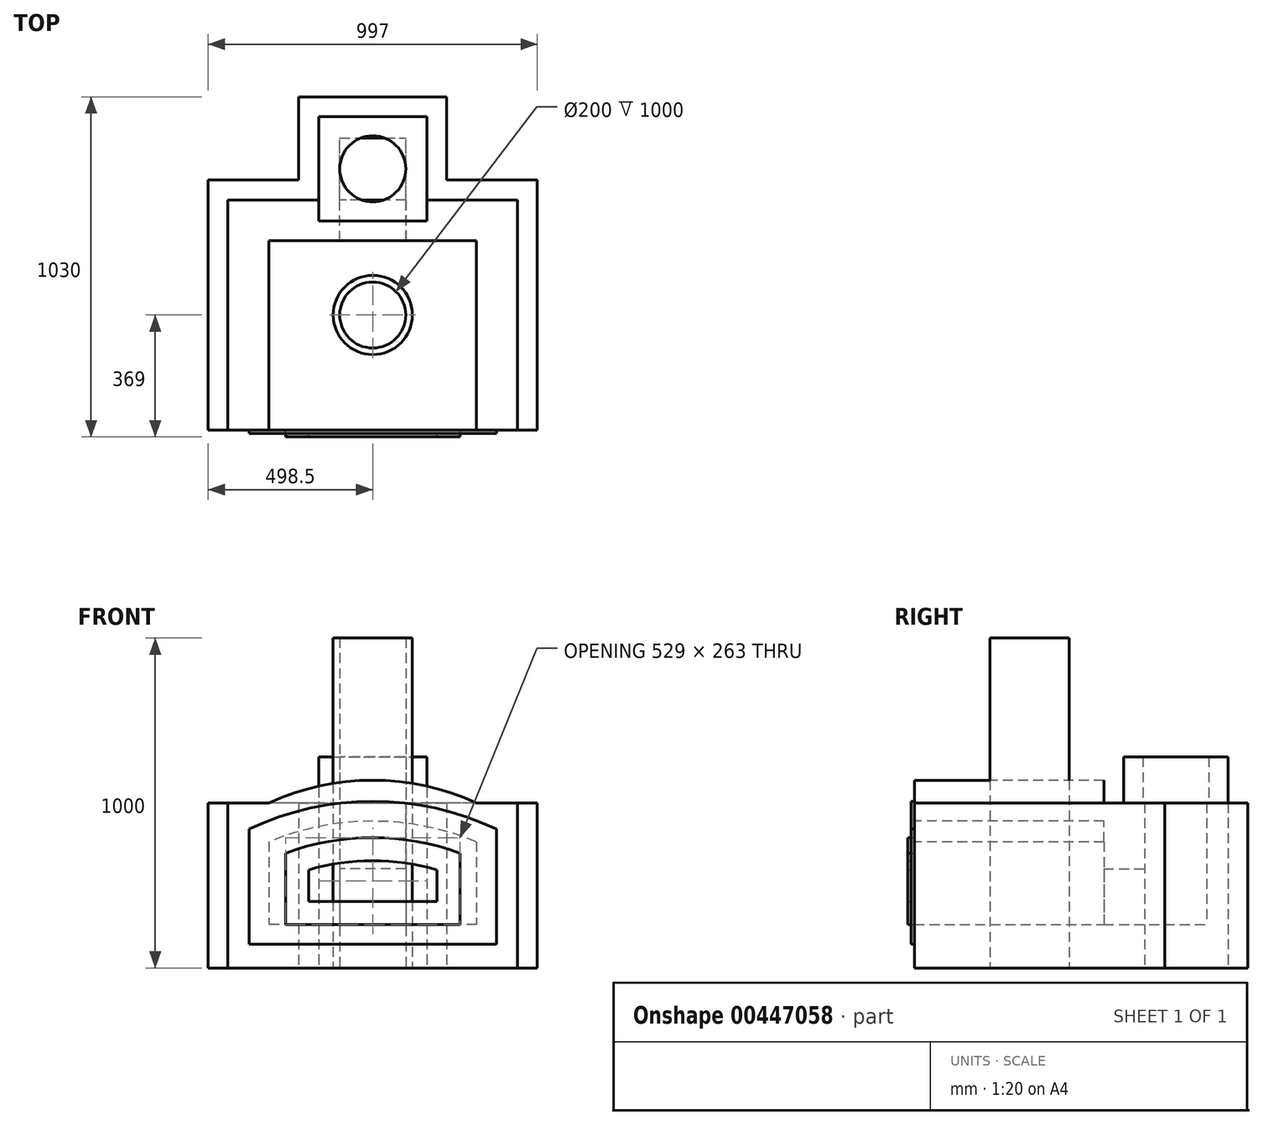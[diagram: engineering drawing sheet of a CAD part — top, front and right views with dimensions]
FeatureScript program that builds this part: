
annotation { "Feature Type Name" : "Feature", "Feature Type Description" : "" }
export const myFeature = defineFeature(function(context is Context, id is Id, definition is map)
    precondition{}
    {
        {
            var Q0;
            Q0=qCreatedBy(makeId("Top.planeOp"),FACE);
            var sketch = newSketch(context, id + "F0", { "sketchPlane" : qUnion([Q0])});
            skLineSegment(sketch, "E0.bottom", {"start": v(438.5, -349) * mm, "end": v(-438.5, -349) * mm});
            skLineSegment(sketch, "E0.top", {"start": v(438.5, 349) * mm, "end": v(164, 349) * mm});
            skLineSegment(sketch, "E0.left", {"start": v(438.5, -349) * mm, "end": v(438.5, 349) * mm});
            skLineSegment(sketch, "E0.right", {"start": v(-438.5, -349) * mm, "end": v(-438.5, 349) * mm});
            skPoint(sketch, "E0.middle", {"position": v(0, 0) * mm});
            skLineSegment(sketch, "E1.top", {"start": v(-164, 601) * mm, "end": v(164, 601) * mm});
            skLineSegment(sketch, "E1.left", {"start": v(-164, 349) * mm, "end": v(-164, 601) * mm});
            skLineSegment(sketch, "E1.right", {"start": v(164, 349) * mm, "end": v(164, 601) * mm});
            skLineSegment(sketch, "E2.trimOffspring", {"start": v(-164, 349) * mm, "end": v(-438.5, 349) * mm});
            skSolve(sketch);
        }
        {
            var Q0;
            Q0=makeQuery(id+"F0.imprint","IMPRINT",FACE,{"disambiguationData":[TD([[makeQuery(id+"F0.imprint","IMPRINT",EDGE,{"derivedFrom":sQuery(id+"F0.wireOp",EDGE,"E0.bottom")}),-1.0]])]});
            extrude(context, id + "F1", {"entities" : qUnion([Q0]), "depth" : (64 + 64 + 4) * mm});
        }
        {
            var Q0;
            Q0=makeQuery(id+"F1.opExtrude","CAP_FACE",FACE,{"disambiguationData":[OSD([sQuery(id+"F0.wireOp",EDGE,"E0.bottom"),sQuery(id+"F0.wireOp",EDGE,"E0.top"),sQuery(id+"F0.wireOp",EDGE,"E0.left"),sQuery(id+"F0.wireOp",EDGE,"E0.right"),sQuery(id+"F0.wireOp",EDGE,"E1.top"),sQuery(id+"F0.wireOp",EDGE,"E1.left"),sQuery(id+"F0.wireOp",EDGE,"E1.right"),sQuery(id+"F0.wireOp",EDGE,"E2.trimOffspring")])],"isStart":false});
            var sketch = newSketch(context, id + "F2", { "sketchPlane" : qUnion([Q0])});
            skLineSegment(sketch, "E3.0", {"start": v(314.5, -474) * mm, "end": v(314.5, 225) * mm});
            skLineSegment(sketch, "E3.1", {"start": v(314.5, 225) * mm, "end": v(100, 225) * mm});
            skLineSegment(sketch, "E3.2", {"start": v(100, 225) * mm, "end": v(100, 537) * mm});
            skLineSegment(sketch, "E3.3", {"start": v(-314.5, -474) * mm, "end": v(-314.5, 225) * mm});
            skLineSegment(sketch, "E3.4", {"start": v(-100, 225) * mm, "end": v(-314.5, 225) * mm});
            skLineSegment(sketch, "E3.5", {"start": v(-100, 225) * mm, "end": v(-100, 537) * mm});
            skLineSegment(sketch, "E3.6", {"start": v(-100, 537) * mm, "end": v(100, 537) * mm});
            skSolve(sketch);
        }
        {
            var Q0;
            {var subQ2=sQuery(id+"F2.wireOp",EDGE,"E3.0");Q0=makeQuery(id+"F2.imprint","IMPRINT",FACE,{"disambiguationData":[TD([[makeQuery(id+"F2.imprint","IMPRINT",EDGE,{"derivedFrom":subQ2}),-1.0]])]});}
            extrude(context, id + "F3", {"entities" : qUnion([Q0]), "operationType" : NewBodyOperationType.ADD, "depth" : (500 - 64 - 64 - 4) * mm});
        }
        {
            var Q0;
            {var subQ0=sQuery(id+"F0.wireOp",EDGE,"E0.bottom");var subQ1=makeQuery(id+"F1.opExtrude","CAP_EDGE",EDGE,{"disambiguationData":[OSD([subQ0])],"isStart":false});Q0=makeQuery(id+"F3.boolean.opBoolean","MERGE",FACE,{"derivedFrom":[makeQuery(id+"F1.opExtrude","SWEPT_FACE",FACE,{"disambiguationData":[OSD([subQ0])]}),makeQuery(id+"F3.opExtrude","SWEPT_FACE",FACE,{"disambiguationData":[OSD([subQ0]),TDD([makeQuery(id+"F2.imprint","IMPRINT",EDGE,{"disambiguationData":[TD([[makeQuery(id+"F2.imprint","INTERSECT",VERTEX,{"derivedFrom":[subQ1,makeQuery(id+"F1.opExtrude","CAP_EDGE",EDGE,{"disambiguationData":[OSD([sQuery(id+"F0.wireOp",EDGE,"E0.left")])],"isStart":false})]}),-1.0]])],"derivedFrom":subQ1})])]}),makeQuery(id+"F3.opExtrude","SWEPT_FACE",FACE,{"disambiguationData":[OSD([subQ0]),TDD([makeQuery(id+"F2.imprint","IMPRINT",EDGE,{"disambiguationData":[TD([[makeQuery(id+"F2.imprint","INTERSECT",VERTEX,{"derivedFrom":[subQ1,makeQuery(id+"F1.opExtrude","CAP_EDGE",EDGE,{"disambiguationData":[OSD([sQuery(id+"F0.wireOp",EDGE,"E0.right")])],"isStart":false})]}),1.0]])],"derivedFrom":subQ1})])]})]});}
            var sketch = newSketch(context, id + "F4", { "sketchPlane" : qUnion([Q0])});
            skLineSegment(sketch, "E4", {"start": v(-314.5, 382) * mm, "end": v(314.5, 382) * mm, "construction": true});
            skLineSegment(sketch, "E5", {"start": v(0, 382) * mm, "end": v(0, 445) * mm, "construction": true});
            skArc(sketch, "E6", {"start": v(314.5, 382) * mm, "mid": v(0, 445) * mm, "end": v(-314.5, 382) * mm});
            skLineSegment(sketch, "E7", {"start": v(0, 569) * mm, "end": v(0, 500) * mm, "construction": true});
            skPoint(sketch, "E7.startSnap0", {"position": v(0, 132) * mm});
            skArc(sketch, "E8", {"start": v(314.5, 500) * mm, "mid": v(0, 569) * mm, "end": v(-314.5, 500) * mm});
            skLineSegment(sketch, "E9", {"start": v(-314.5, 500) * mm, "end": v(-314.5, 382) * mm});
            skLineSegment(sketch, "E10", {"start": v(314.5, 500) * mm, "end": v(314.5, 382) * mm});
            skSolve(sketch);
        }
        {
            var Q0;
            Q0=makeQuery(id+"F4.imprint","IMPRINT",FACE,{"disambiguationData":[TD([[makeQuery(id+"F4.imprint","IMPRINT",EDGE,{"derivedFrom":sQuery(id+"F4.wireOp",EDGE,"E6")}),-1.0]])]});
            var Q1;
            Q1=makeQuery(id+"F3.opExtrude","SWEPT_FACE",FACE,{"disambiguationData":[OSD([sQuery(id+"F2.wireOp",EDGE,"E3.4")])]});
            extrude(context, id + "F5", {"entities" : qUnion([Q0]), "operationType" : NewBodyOperationType.ADD, "endBound" : BoundingType.UP_TO_SURFACE, "oppositeDirection" : true, "endBoundEntityFace" : qUnion([Q1]), "depth" : 25 * mm});
        }
        {
            var Q0;
            Q0=makeQuery(id+"F3.opExtrude","SWEPT_FACE",FACE,{"disambiguationData":[OSD([sQuery(id+"F2.wireOp",EDGE,"E3.5")])]});
            var sketch = newSketch(context, id + "F6", { "sketchPlane" : qUnion([Q0])});
            skLineSegment(sketch, "E11.bottom", {"start": v(225, 500) * mm, "end": v(349, 500) * mm});
            skLineSegment(sketch, "E11.top", {"start": v(225, 300) * mm, "end": v(349, 300) * mm});
            skLineSegment(sketch, "E11.left", {"start": v(225, 500) * mm, "end": v(225, 300) * mm});
            skLineSegment(sketch, "E11.right", {"start": v(349, 500) * mm, "end": v(349, 300) * mm});
            skSolve(sketch);
        }
        {
            var Q0;
            {var subQ5=sQuery(id+"F6.wireOp",EDGE,"E11.bottom");Q0=makeQuery(id+"F6.imprint","IMPRINT",FACE,{"disambiguationData":[TD([[makeQuery(id+"F6.imprint","IMPRINT",EDGE,{"derivedFrom":subQ5}),-1.0]])]});}
            var Q1;
            Q1=makeQuery(id+"F3.opExtrude","SWEPT_FACE",FACE,{"disambiguationData":[OSD([sQuery(id+"F2.wireOp",EDGE,"E3.2")])]});
            extrude(context, id + "F7", {"entities" : qUnion([Q0]), "operationType" : NewBodyOperationType.ADD, "endBound" : BoundingType.UP_TO_SURFACE, "endBoundEntityFace" : qUnion([Q1]), "depth" : 25 * mm});
        }
        {
            var Q0;
            Q0=makeQuery(id+"F7.boolean.opBoolean","MERGE",FACE,{"derivedFrom":[makeQuery(id+"F3.opExtrude","CAP_FACE",FACE,{"disambiguationData":[OSD([sQuery(id+"F0.wireOp",EDGE,"E0.bottom"),sQuery(id+"F0.wireOp",EDGE,"E0.top"),sQuery(id+"F0.wireOp",EDGE,"E0.left"),sQuery(id+"F0.wireOp",EDGE,"E0.right"),sQuery(id+"F0.wireOp",EDGE,"E1.top"),sQuery(id+"F0.wireOp",EDGE,"E1.left"),sQuery(id+"F0.wireOp",EDGE,"E1.right"),sQuery(id+"F0.wireOp",EDGE,"E2.trimOffspring"),sQuery(id+"F2.wireOp",EDGE,"E3.0"),sQuery(id+"F2.wireOp",EDGE,"E3.1"),sQuery(id+"F2.wireOp",EDGE,"E3.2"),sQuery(id+"F2.wireOp",EDGE,"E3.3"),sQuery(id+"F2.wireOp",EDGE,"E3.4"),sQuery(id+"F2.wireOp",EDGE,"E3.5"),sQuery(id+"F2.wireOp",EDGE,"E3.6")])],"isStart":false}),makeQuery(id+"F7.opExtrude","SWEPT_FACE",FACE,{"disambiguationData":[OSD([sQuery(id+"F6.wireOp",EDGE,"E11.bottom")])]})]});
            var sketch = newSketch(context, id + "F8", { "sketchPlane" : qUnion([Q0])});
            skLineSegment(sketch, "E12.bottom", {"start": v(-164, 601) * mm, "end": v(164, 601) * mm});
            skLineSegment(sketch, "E12.top", {"start": v(-164, 285) * mm, "end": v(164, 285) * mm});
            skLineSegment(sketch, "E12.left", {"start": v(-164, 601) * mm, "end": v(-164, 285) * mm});
            skLineSegment(sketch, "E12.right", {"start": v(164, 601) * mm, "end": v(164, 285) * mm});
            skCircle(sketch, "E13", {"center": v(0, 443) * mm, "radius": 100 * mm});
            skPoint(sketch, "E13.centerSnap0", {"position": v(100, 443) * mm});
            skPoint(sketch, "E13.centerSnap1", {"position": v(0, 349) * mm});
            skSolve(sketch);
        }
        {
            var Q0;
            {var subQ0=sQuery(id+"F8.wireOp",EDGE,"E13");var subQ1=makeQuery(id+"F3.opExtrude","CAP_EDGE",EDGE,{"disambiguationData":[OSD([sQuery(id+"F2.wireOp",EDGE,"E3.6")])],"isStart":false});var subQ2=makeQuery(id+"F8.imprint","INTERSECT",VERTEX,{"disambiguationData":[OD(1.0)],"derivedFrom":[subQ1,subQ0]});Q0=makeQuery(id+"F8.imprint","IMPRINT",FACE,{"disambiguationData":[TD([[makeQuery(id+"F8.imprint","IMPRINT",EDGE,{"disambiguationData":[TD([[subQ2,-1.0]])],"derivedFrom":subQ0}),-1.0]])]});}
            var Q1;
            {var subQ18=sQuery(id+"F8.wireOp",EDGE,"E12.bottom");Q1=makeQuery(id+"F8.imprint","IMPRINT",FACE,{"disambiguationData":[TD([[makeQuery(id+"F8.imprint","IMPRINT",EDGE,{"derivedFrom":subQ18}),-1.0]])]});}
            var Q2;
            {var subQ0=sQuery(id+"F8.wireOp",EDGE,"E13");var subQ1=makeQuery(id+"F3.opExtrude","CAP_EDGE",EDGE,{"disambiguationData":[OSD([sQuery(id+"F2.wireOp",EDGE,"E3.2")])],"isStart":false});var subQ2=makeQuery(id+"F8.imprint","INTERSECT",VERTEX,{"derivedFrom":[subQ1,subQ0]});Q2=makeQuery(id+"F8.imprint","IMPRINT",FACE,{"disambiguationData":[TD([[makeQuery(id+"F8.imprint","IMPRINT",EDGE,{"disambiguationData":[TD([[subQ2,1.0]])],"derivedFrom":subQ0}),-1.0]])]});}
            var Q3;
            {var subQ0=sQuery(id+"F8.wireOp",EDGE,"E13");var subQ1=makeQuery(id+"F3.opExtrude","CAP_EDGE",EDGE,{"disambiguationData":[OSD([sQuery(id+"F2.wireOp",EDGE,"E3.6")])],"isStart":false});var subQ2=makeQuery(id+"F8.imprint","INTERSECT",VERTEX,{"disambiguationData":[OD(0.0)],"derivedFrom":[subQ1,subQ0]});Q3=makeQuery(id+"F8.imprint","IMPRINT",FACE,{"disambiguationData":[TD([[makeQuery(id+"F8.imprint","IMPRINT",EDGE,{"disambiguationData":[TD([[subQ2,1.0]])],"derivedFrom":subQ0}),-1.0]])]});}
            var Q4;
            {var subQ0=sQuery(id+"F8.wireOp",EDGE,"E13");var subQ1=sQuery(id+"F2.wireOp",EDGE,"E3.5");var subQ2=makeQuery(id+"F3.opExtrude","CAP_EDGE",EDGE,{"disambiguationData":[OSD([subQ1])],"isStart":false});var subQ3=makeQuery(id+"F8.imprint","INTERSECT",VERTEX,{"derivedFrom":[subQ2,subQ0]});Q4=makeQuery(id+"F8.imprint","IMPRINT",FACE,{"disambiguationData":[TD([[makeQuery(id+"F8.imprint","IMPRINT",EDGE,{"disambiguationData":[TD([[subQ3,-1.0]])],"derivedFrom":subQ0}),-1.0]])]});}
            extrude(context, id + "F9", {"entities" : qUnion([Q0, Q1, Q2, Q3, Q4]), "operationType" : NewBodyOperationType.ADD, "depth" : (89 + 50) * mm});
        }
        {
            var Q0;
            Q0=qCreatedBy(makeId("Top.planeOp"),FACE);
            var sketch = newSketch(context, id + "F10", { "sketchPlane" : qUnion([Q0])});
            skCircle(sketch, "E14", {"center": v(0, 0) * mm, "radius": 120 * mm});
            skCircle(sketch, "E15", {"center": v(0, 0) * mm, "radius": 100 * mm});
            skSolve(sketch);
        }
        {
            var Q0;
            Q0=makeQuery(id+"F10.imprint","IMPRINT",FACE,{"disambiguationData":[TD([[makeQuery(id+"F10.imprint","IMPRINT",EDGE,{"derivedFrom":sQuery(id+"F10.wireOp",EDGE,"E14")}),1.0]])]});
            extrude(context, id + "F11", {"entities" : qUnion([Q0]), "depth" : 1000 * mm});
        }
        {
            var Q0;
            Q0=makeQuery(id+"F1.opExtrude","CAP_FACE",FACE,{"disambiguationData":[OSD([sQuery(id+"F0.wireOp",EDGE,"E0.bottom"),sQuery(id+"F0.wireOp",EDGE,"E0.top"),sQuery(id+"F0.wireOp",EDGE,"E0.left"),sQuery(id+"F0.wireOp",EDGE,"E0.right"),sQuery(id+"F0.wireOp",EDGE,"E1.top"),sQuery(id+"F0.wireOp",EDGE,"E1.left"),sQuery(id+"F0.wireOp",EDGE,"E1.right"),sQuery(id+"F0.wireOp",EDGE,"E2.trimOffspring")])],"isStart":true});
            var sketch = newSketch(context, id + "F12", { "sketchPlane" : qUnion([Q0])});
            skLineSegment(sketch, "E16.0", {"start": v(498.5, 349) * mm, "end": v(498.5, -409) * mm});
            skLineSegment(sketch, "E16.1", {"start": v(498.5, -409) * mm, "end": v(224, -409) * mm});
            skLineSegment(sketch, "E16.2", {"start": v(224, -409) * mm, "end": v(224, -661) * mm});
            skLineSegment(sketch, "E16.3", {"start": v(-498.5, 349) * mm, "end": v(-498.5, -409) * mm});
            skLineSegment(sketch, "E16.4", {"start": v(-224, -409) * mm, "end": v(-498.5, -409) * mm});
            skLineSegment(sketch, "E16.5", {"start": v(-224, -409) * mm, "end": v(-224, -661) * mm});
            skLineSegment(sketch, "E16.6", {"start": v(-224, -661) * mm, "end": v(224, -661) * mm});
            skLineSegment(sketch, "E17", {"start": v(-438.5, 349) * mm, "end": v(-498.5, 349) * mm});
            skLineSegment(sketch, "E18", {"start": v(438.5, 349) * mm, "end": v(498.5, 349) * mm});
            skSolve(sketch);
        }
        {
            var Q0;
            Q0=makeQuery(id+"F12.imprint","IMPRINT",FACE,{"disambiguationData":[TD([[makeQuery(id+"F12.imprint","IMPRINT",EDGE,{"derivedFrom":sQuery(id+"F12.wireOp",EDGE,"E16.0")}),-1.0]])]});
            extrude(context, id + "F13", {"entities" : qUnion([Q0]), "oppositeDirection" : true, "depth" : 500 * mm});
        }
        {
            var Q0;
            {var subQ0=sQuery(id+"F0.wireOp",EDGE,"E0.bottom");var subQ1=makeQuery(id+"F1.opExtrude","CAP_EDGE",EDGE,{"disambiguationData":[OSD([subQ0])],"isStart":false});Q0=makeQuery(id+"F5.boolean.opBoolean","MERGE",FACE,{"derivedFrom":[makeQuery(id+"F3.boolean.opBoolean","MERGE",FACE,{"derivedFrom":[makeQuery(id+"F1.opExtrude","SWEPT_FACE",FACE,{"disambiguationData":[OSD([subQ0])]}),makeQuery(id+"F3.opExtrude","SWEPT_FACE",FACE,{"disambiguationData":[OSD([subQ0]),TDD([makeQuery(id+"F2.imprint","IMPRINT",EDGE,{"disambiguationData":[TD([[makeQuery(id+"F2.imprint","INTERSECT",VERTEX,{"derivedFrom":[subQ1,makeQuery(id+"F1.opExtrude","CAP_EDGE",EDGE,{"disambiguationData":[OSD([sQuery(id+"F0.wireOp",EDGE,"E0.left")])],"isStart":false})]}),-1.0]])],"derivedFrom":subQ1})])]}),makeQuery(id+"F3.opExtrude","SWEPT_FACE",FACE,{"disambiguationData":[OSD([subQ0]),TDD([makeQuery(id+"F2.imprint","IMPRINT",EDGE,{"disambiguationData":[TD([[makeQuery(id+"F2.imprint","INTERSECT",VERTEX,{"derivedFrom":[subQ1,makeQuery(id+"F1.opExtrude","CAP_EDGE",EDGE,{"disambiguationData":[OSD([sQuery(id+"F0.wireOp",EDGE,"E0.right")])],"isStart":false})]}),1.0]])],"derivedFrom":subQ1})])]})]}),makeQuery(id+"F5.opExtrude","CAP_FACE",FACE,{"disambiguationData":[OSD([sQuery(id+"F4.wireOp",EDGE,"E6"),sQuery(id+"F4.wireOp",EDGE,"E8"),sQuery(id+"F4.wireOp",EDGE,"E9"),sQuery(id+"F4.wireOp",EDGE,"E10")])],"isStart":true})]});}
            var sketch = newSketch(context, id + "F14", { "sketchPlane" : qUnion([Q0])});
            skArc(sketch, "E19.0", {"start": v(374.5, 420.97) * mm, "mid": v(0, 505) * mm, "end": v(-374.5, 420.97) * mm});
            skLineSegment(sketch, "E19.1", {"start": v(374.5, 420.97) * mm, "end": v(374.5, 72) * mm});
            skLineSegment(sketch, "E19.2", {"start": v(374.5, 72) * mm, "end": v(-374.5, 72) * mm});
            skLineSegment(sketch, "E19.3", {"start": v(-374.5, 420.97) * mm, "end": v(-374.5, 72) * mm});
            skLineSegment(sketch, "E20.0", {"start": v(-264.5, 347.92) * mm, "end": v(-264.5, 132) * mm});
            skArc(sketch, "E20.1", {"start": v(264.5, 347.92) * mm, "mid": v(0, 395) * mm, "end": v(-264.5, 347.92) * mm});
            skLineSegment(sketch, "E20.2", {"start": v(264.5, 347.92) * mm, "end": v(264.5, 132) * mm});
            skLineSegment(sketch, "E21", {"start": v(-264.5, 132) * mm, "end": v(264.5, 132) * mm});
            skSolve(sketch);
        }
        {
            var Q0;
            Q0=makeQuery(id+"F14.imprint","IMPRINT",FACE,{"disambiguationData":[TD([[makeQuery(id+"F14.imprint","IMPRINT",EDGE,{"derivedFrom":sQuery(id+"F14.wireOp",EDGE,"E19.0")}),1.0]])]});
            var Q1;
            {var subQ6=sQuery(id+"F14.wireOp",EDGE,"E20.0");Q1=makeQuery(id+"F14.imprint","IMPRINT",FACE,{"disambiguationData":[TD([[makeQuery(id+"F14.imprint","IMPRINT",EDGE,{"derivedFrom":subQ6}),-1.0]])]});}
            extrude(context, id + "F15", {"entities" : qUnion([Q0, Q1]), "depth" : 10 * mm});
        }
        {
            var Q0;
            Q0=makeQuery(id+"F15.opExtrude","CAP_FACE",FACE,{"disambiguationData":[OSD([sQuery(id+"F14.wireOp",EDGE,"E19.0"),sQuery(id+"F14.wireOp",EDGE,"E19.1"),sQuery(id+"F14.wireOp",EDGE,"E19.2"),sQuery(id+"F14.wireOp",EDGE,"E19.3"),sQuery(id+"F14.wireOp",EDGE,"E20.0"),sQuery(id+"F14.wireOp",EDGE,"E20.1"),sQuery(id+"F14.wireOp",EDGE,"E20.2"),sQuery(id+"F14.wireOp",EDGE,"E21")])],"isStart":false});
            var sketch = newSketch(context, id + "F16", { "sketchPlane" : qUnion([Q0])});
            skArc(sketch, "E22.0", {"start": v(194.5, 297.3) * mm, "mid": v(0, 325) * mm, "end": v(-194.5, 297.3) * mm});
            skLineSegment(sketch, "E22.1", {"start": v(194.5, 297.3) * mm, "end": v(194.5, 202) * mm});
            skLineSegment(sketch, "E22.2", {"start": v(194.5, 202) * mm, "end": v(-194.5, 202) * mm});
            skLineSegment(sketch, "E22.3", {"start": v(-194.5, 297.3) * mm, "end": v(-194.5, 202) * mm});
            skSolve(sketch);
        }
        {
            var Q0;
            Q0=makeQuery(id+"F16.imprint","IMPRINT",FACE,{"disambiguationData":[TD([[makeQuery(id+"F16.imprint","IMPRINT",EDGE,{"derivedFrom":sQuery(id+"F16.wireOp",EDGE,"E22.0")}),-1.0]])]});
            extrude(context, id + "F17", {"entities" : qUnion([Q0]), "depth" : 10 * mm});
        }
    });
